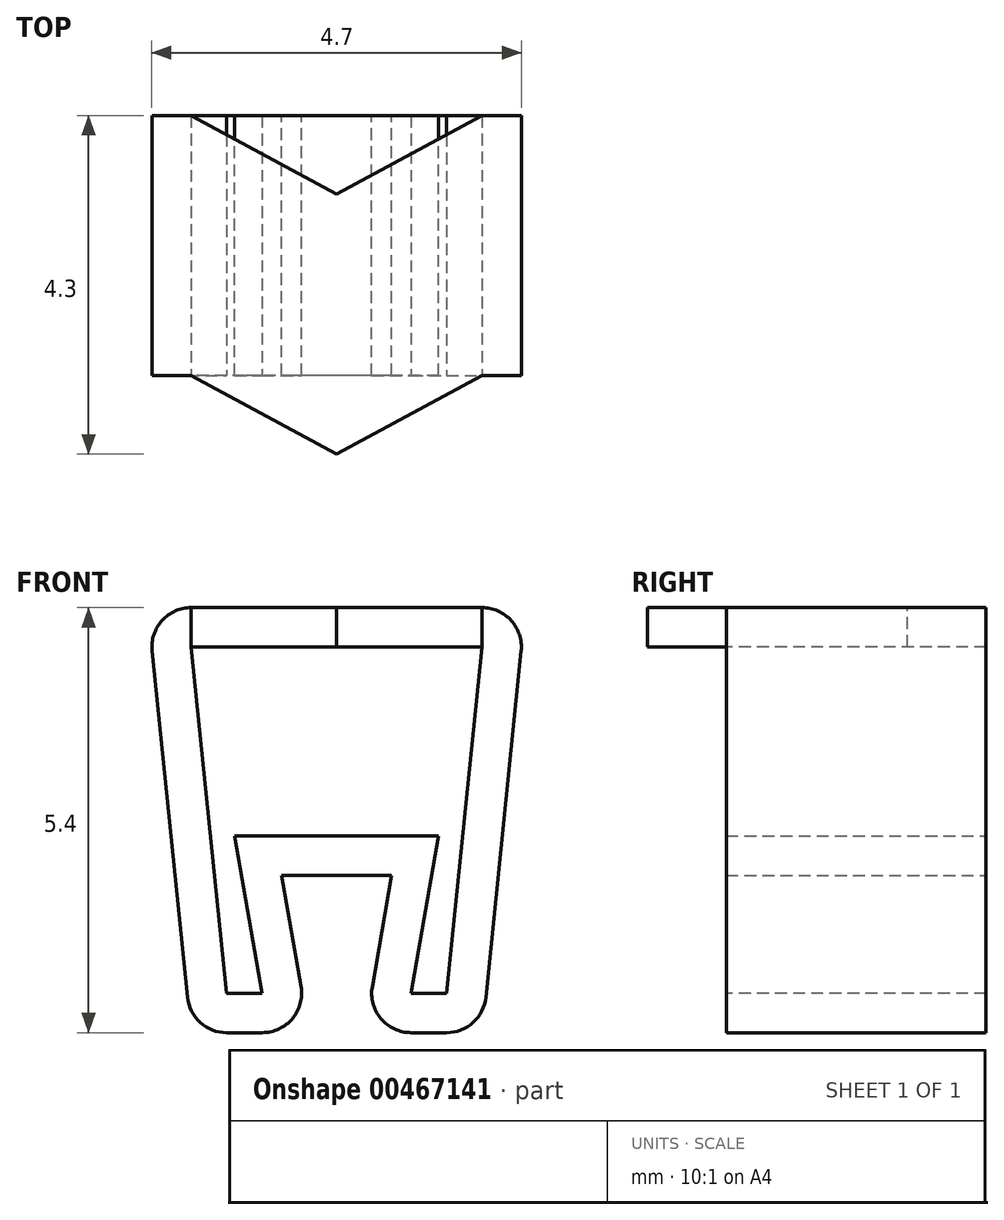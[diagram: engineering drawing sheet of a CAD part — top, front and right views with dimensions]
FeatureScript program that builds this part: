
annotation { "Feature Type Name" : "Feature", "Feature Type Description" : "" }
export const myFeature = defineFeature(function(context is Context, id is Id, definition is map)
    precondition{}
    {
        {
            var Q0;
            Q0=qCreatedBy(makeId("Front.planeOp"),FACE);
            var sketch = newSketch(context, id + "F0", { "sketchPlane" : qUnion([Q0])});
            skLineSegment(sketch, "E0", {"start": v(0, -2.4) * mm, "end": v(-0.7, -2.4) * mm});
            skLineSegment(sketch, "E1", {"start": v(-0.7, -2.4) * mm, "end": v(-0.35, -4.4) * mm});
            skLineSegment(sketch, "E2", {"start": v(-0.35, -4.4) * mm, "end": v(-1.85, -4.4) * mm});
            skLineSegment(sketch, "E3", {"start": v(-1.85, -4.4) * mm, "end": v(-2.4, 1) * mm});
            skLineSegment(sketch, "E4", {"start": v(-2.4, 1) * mm, "end": v(0, 1) * mm});
            skLineSegment(sketch, "E5.MirrorCS", {"start": v(0, -2.4) * mm, "end": v(0.7, -2.4) * mm});
            skLineSegment(sketch, "E6.MirrorCS", {"start": v(0.7, -2.4) * mm, "end": v(0.35, -4.4) * mm});
            skLineSegment(sketch, "E7.MirrorCS", {"start": v(2.4, 1) * mm, "end": v(0, 1) * mm});
            skLineSegment(sketch, "E8.MirrorCS", {"start": v(1.85, -4.4) * mm, "end": v(2.4, 1) * mm});
            skLineSegment(sketch, "E9.MirrorCS", {"start": v(0.35, -4.4) * mm, "end": v(1.85, -4.4) * mm});
            skSolve(sketch);
        }
        {
            var Q0;
            Q0 = qSketchRegion(id + "F0", true);
            extrude(context, id + "F1", {"entities" : qUnion([Q0]), "depth" : 3.3 * mm});
        }
        {
            var Q0;
            Q0=makeQuery(id+"F1.opExtrude","SWEPT_EDGE",EDGE,{"disambiguationData":[OSD([sQuery(id+"F0.wireOp",EDGE,"E7.MirrorCS"),sQuery(id+"F0.wireOp",EDGE,"E8.MirrorCS")])]});
            var Q1;
            Q1=makeQuery(id+"F1.opExtrude","SWEPT_EDGE",EDGE,{"disambiguationData":[OSD([sQuery(id+"F0.wireOp",EDGE,"E8.MirrorCS"),sQuery(id+"F0.wireOp",EDGE,"E9.MirrorCS")])]});
            var Q2;
            Q2=makeQuery(id+"F1.opExtrude","SWEPT_EDGE",EDGE,{"disambiguationData":[OSD([sQuery(id+"F0.wireOp",EDGE,"E1"),sQuery(id+"F0.wireOp",EDGE,"E2")])]});
            var Q3;
            Q3=makeQuery(id+"F1.opExtrude","SWEPT_EDGE",EDGE,{"disambiguationData":[OSD([sQuery(id+"F0.wireOp",EDGE,"E3"),sQuery(id+"F0.wireOp",EDGE,"E4")])]});
            var Q4;
            Q4=makeQuery(id+"F1.opExtrude","SWEPT_EDGE",EDGE,{"disambiguationData":[OSD([sQuery(id+"F0.wireOp",EDGE,"E6.MirrorCS"),sQuery(id+"F0.wireOp",EDGE,"E9.MirrorCS")])]});
            var Q5;
            Q5=makeQuery(id+"F1.opExtrude","SWEPT_EDGE",EDGE,{"disambiguationData":[OSD([sQuery(id+"F0.wireOp",EDGE,"E2"),sQuery(id+"F0.wireOp",EDGE,"E3")])]});
            fillet(context, id + "F2", {"entities" : qUnion([Q0, Q1, Q2, Q3, Q4, Q5]), "radius" : 0.5 * mm, "tangentPropagation" : true, "allowEdgeOverflow" : false});
        }
        {
            var Q0;
            Q0=makeQuery(id+"F1.opExtrude","CAP_FACE",FACE,{"disambiguationData":[OSD([sQuery(id+"F0.wireOp",EDGE,"E0"),sQuery(id+"F0.wireOp",EDGE,"E1"),sQuery(id+"F0.wireOp",EDGE,"E2"),sQuery(id+"F0.wireOp",EDGE,"E3"),sQuery(id+"F0.wireOp",EDGE,"E4"),sQuery(id+"F0.wireOp",EDGE,"E5.MirrorCS"),sQuery(id+"F0.wireOp",EDGE,"E6.MirrorCS"),sQuery(id+"F0.wireOp",EDGE,"E7.MirrorCS"),sQuery(id+"F0.wireOp",EDGE,"E8.MirrorCS"),sQuery(id+"F0.wireOp",EDGE,"E9.MirrorCS")])],"isStart":false});
            var Q1;
            Q1=makeQuery(id+"F1.opExtrude","CAP_FACE",FACE,{"disambiguationData":[OSD([sQuery(id+"F0.wireOp",EDGE,"E0"),sQuery(id+"F0.wireOp",EDGE,"E1"),sQuery(id+"F0.wireOp",EDGE,"E2"),sQuery(id+"F0.wireOp",EDGE,"E3"),sQuery(id+"F0.wireOp",EDGE,"E4"),sQuery(id+"F0.wireOp",EDGE,"E5.MirrorCS"),sQuery(id+"F0.wireOp",EDGE,"E6.MirrorCS"),sQuery(id+"F0.wireOp",EDGE,"E7.MirrorCS"),sQuery(id+"F0.wireOp",EDGE,"E8.MirrorCS"),sQuery(id+"F0.wireOp",EDGE,"E9.MirrorCS")])],"isStart":true});
            shell(context, id + "F3", {"entities" : qUnion([Q0, Q1]), "thickness" : 0.5 * mm});
        }
        {
            var Q0;
            Q0=makeQuery(id+"F1.opExtrude","SWEPT_FACE",FACE,{"disambiguationData":[OSD([sQuery(id+"F0.wireOp",EDGE,"E4"),sQuery(id+"F0.wireOp",EDGE,"E7.MirrorCS")])]});
            var sketch = newSketch(context, id + "F4", { "sketchPlane" : qUnion([Q0])});
            skLineSegment(sketch, "E10", {"start": v(-1.85, -3.3) * mm, "end": v(0, -4.3) * mm});
            skLineSegment(sketch, "E11", {"start": v(0, -4.3) * mm, "end": v(1.85, -3.3) * mm});
            skLineSegment(sketch, "E12", {"start": v(-1.85, 0) * mm, "end": v(0, -1) * mm});
            skLineSegment(sketch, "E13", {"start": v(0, -1) * mm, "end": v(1.85, 0) * mm});
            skSolve(sketch);
        }
        {
            var Q0;
            Q0=makeQuery(id+"F4.imprint","IMPRINT",FACE,{"disambiguationData":[TD([[makeQuery(id+"F4.imprint","IMPRINT",EDGE,{"derivedFrom":sQuery(id+"F4.wireOp",EDGE,"E10")}),1.0]])]});
            var Q1;
            Q1=makeQuery(id+"F3.opShell","OFFSET_FACE",FACE,{"disambiguationData":[OSD([sQuery(id+"F0.wireOp",EDGE,"E4"),sQuery(id+"F0.wireOp",EDGE,"E7.MirrorCS")])]});
            extrude(context, id + "F5", {"entities" : qUnion([Q0]), "operationType" : NewBodyOperationType.ADD, "endBound" : BoundingType.UP_TO_SURFACE, "oppositeDirection" : true, "endBoundEntityFace" : qUnion([Q1]), "depth" : 25 * mm});
        }
        {
            var Q0;
            Q0=makeQuery(id+"F4.imprint","IMPRINT",FACE,{"disambiguationData":[TD([[makeQuery(id+"F4.imprint","IMPRINT",EDGE,{"derivedFrom":sQuery(id+"F4.wireOp",EDGE,"E12")}),1.0]])]});
            var Q1;
            {var subQ0=sQuery(id+"F0.wireOp",EDGE,"E7.MirrorCS");var subQ1=sQuery(id+"F0.wireOp",EDGE,"E4");Q1=makeQuery(id+"F5.boolean.opBoolean","MERGE",FACE,{"derivedFrom":[makeQuery(id+"F3.opShell","OFFSET_FACE",FACE,{"disambiguationData":[OSD([subQ1,subQ0])]}),makeQuery(id+"F5.opExtrude","CAP_FACE",FACE,{"disambiguationData":[OSD([subQ1,subQ0])],"isStart":false})]});}
            extrude(context, id + "F6", {"entities" : qUnion([Q0]), "operationType" : NewBodyOperationType.REMOVE, "endBound" : BoundingType.UP_TO_SURFACE, "oppositeDirection" : true, "endBoundEntityFace" : qUnion([Q1]), "depth" : 25 * mm});
        }
    });
